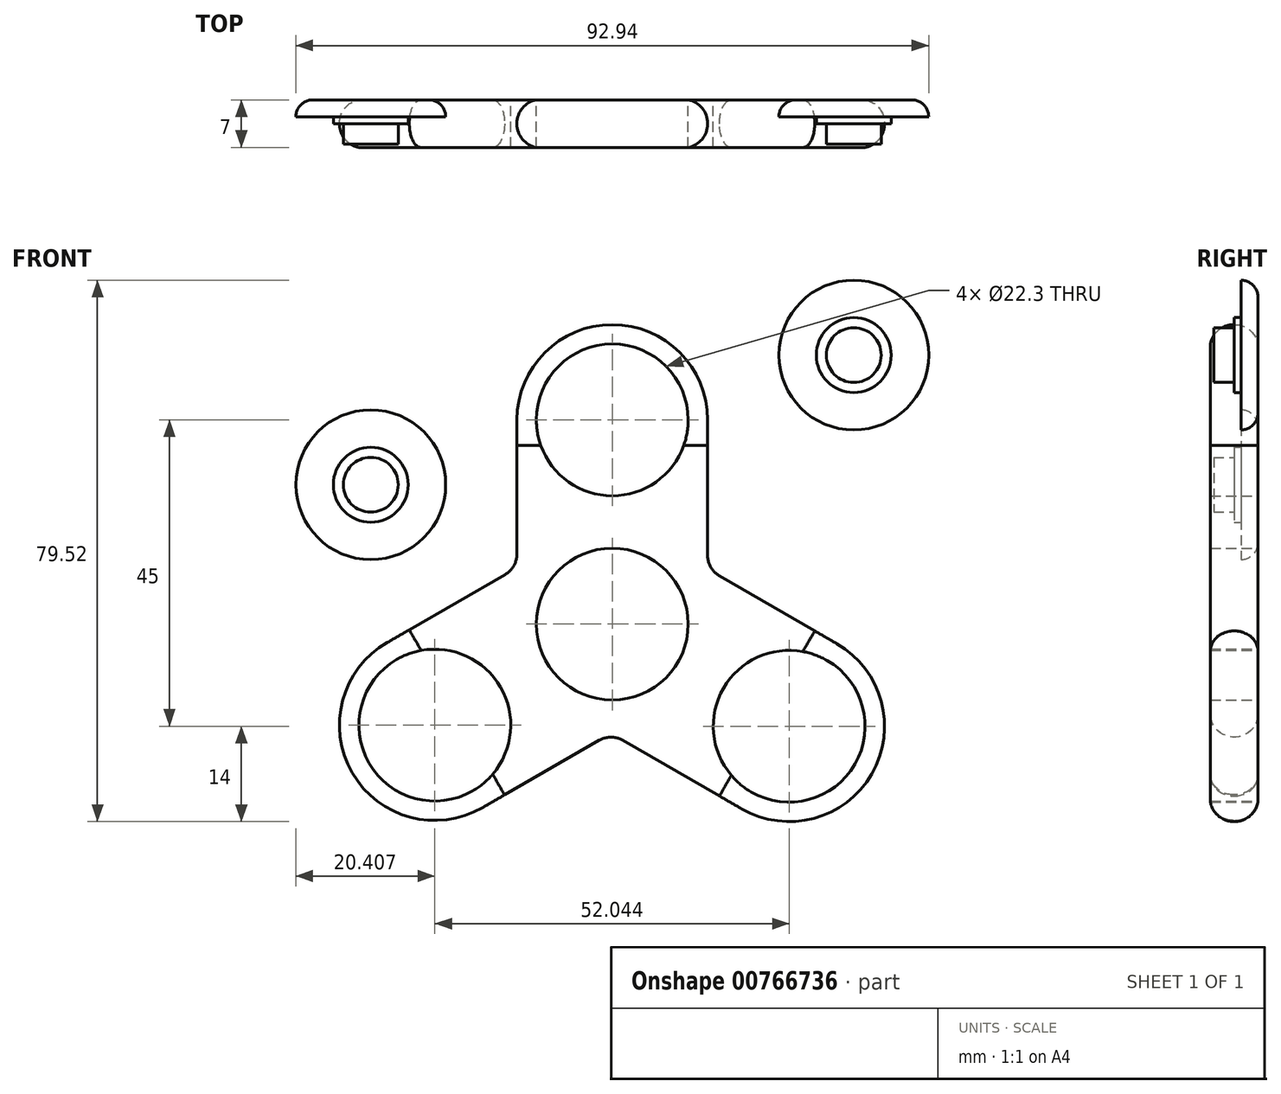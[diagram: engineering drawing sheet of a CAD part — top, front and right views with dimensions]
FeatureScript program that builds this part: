
annotation { "Feature Type Name" : "Feature", "Feature Type Description" : "" }
export const myFeature = defineFeature(function(context is Context, id is Id, definition is map)
    precondition{}
    {
        {
            var Q0;
            Q0=qCreatedBy(makeId("Front.planeOp"),FACE);
            var sketch = newSketch(context, id + "F0", { "sketchPlane" : qUnion([Q0])});
            skLineSegment(sketch, "E0.left", {"start": v(-14, -6.7) * mm, "end": v(-14, 15) * mm});
            skLineSegment(sketch, "E0.right", {"start": v(14, -6.92) * mm, "end": v(14, 15) * mm});
            skPoint(sketch, "E0.middle", {"position": v(0, 0) * mm});
            skArc(sketch, "E1", {"start": v(14, 15) * mm, "mid": v(0, 29) * mm, "end": v(-14, 15) * mm});
            skLineSegment(sketch, "E2.right", {"start": v(-0.18, -31.06) * mm, "end": v(18.98, -42.12) * mm});
            skArc(sketch, "E3", {"start": v(18.98, -42.12) * mm, "mid": v(38.1, -37) * mm, "end": v(32.98, -17.88) * mm});
            skLineSegment(sketch, "E4.right", {"start": v(-14, -6.7) * mm, "end": v(-33.06, -17.71) * mm});
            skArc(sketch, "E5", {"start": v(-33.06, -17.71) * mm, "mid": v(-38.19, -36.84) * mm, "end": v(-19.06, -41.96) * mm});
            skLineSegment(sketch, "E6.trimOffspring", {"start": v(-0.18, -31.06) * mm, "end": v(-19.06, -41.96) * mm});
            skLineSegment(sketch, "E7.trimOffspring", {"start": v(14, -6.92) * mm, "end": v(32.98, -17.88) * mm});
            skCircle(sketch, "E8", {"center": v(0, -15) * mm, "radius": 11.15 * mm});
            skCircle(sketch, "E9", {"center": v(-26.06, -29.84) * mm, "radius": 11.15 * mm});
            skCircle(sketch, "E10", {"center": v(25.98, -30) * mm, "radius": 11.15 * mm});
            skCircle(sketch, "E11", {"center": v(0, 15) * mm, "radius": 11.15 * mm});
            skSolve(sketch);
        }
        {
            var Q0;
            Q0=makeQuery(id+"F0.imprint","IMPRINT",FACE,{"disambiguationData":[TD([[makeQuery(id+"F0.imprint","IMPRINT",EDGE,{"derivedFrom":sQuery(id+"F0.wireOp",EDGE,"E0.left")}),-1.0]])]});
            extrude(context, id + "F1", {"entities" : qUnion([Q0]), "depth" : 7 * mm, "offsetDistance" : 25 * mm});
        }
        {
            var Q0;
            Q0=qCreatedBy(makeId("Front.planeOp"),FACE);
            var sketch = newSketch(context, id + "F2", { "sketchPlane" : qUnion([Q0])});
            skCircle(sketch, "E12", {"center": v(35.47, 24.52) * mm, "radius": 11 * mm});
            skCircle(sketch, "E13", {"center": v(35.47, 24.52) * mm, "radius": 5.5 * mm});
            skCircle(sketch, "E14", {"center": v(35.47, 24.52) * mm, "radius": 4.03 * mm});
            skSolve(sketch);
        }
        {
            var Q0;
            Q0=makeQuery(id+"F2.imprint","IMPRINT",FACE,{"disambiguationData":[TD([[makeQuery(id+"F2.imprint","IMPRINT",EDGE,{"derivedFrom":sQuery(id+"F2.wireOp",EDGE,"E12")}),1.0]])]});
            extrude(context, id + "F3", {"entities" : qUnion([Q0]), "depth" : 2.5 * mm, "offsetDistance" : 25 * mm});
        }
        {
            var Q0;
            Q0=makeQuery(id+"F2.imprint","IMPRINT",FACE,{"disambiguationData":[TD([[makeQuery(id+"F2.imprint","IMPRINT",EDGE,{"derivedFrom":sQuery(id+"F2.wireOp",EDGE,"E13")}),1.0]])]});
            extrude(context, id + "F4", {"entities" : qUnion([Q0]), "operationType" : NewBodyOperationType.ADD, "depth" : 3.5 * mm, "offsetDistance" : 25 * mm});
        }
        {
            var Q0;
            Q0=makeQuery(id+"F2.imprint","IMPRINT",FACE,{"disambiguationData":[TD([[makeQuery(id+"F2.imprint","IMPRINT",EDGE,{"derivedFrom":sQuery(id+"F2.wireOp",EDGE,"E14")}),1.0]])]});
            extrude(context, id + "F5", {"entities" : qUnion([Q0]), "operationType" : NewBodyOperationType.ADD, "depth" : 6.5 * mm, "offsetDistance" : 25 * mm});
        }
        {
            var Q0;
            Q0=makeQuery(id+"F1.opExtrude","SWEPT_FACE",FACE,{"disambiguationData":[OSD([sQuery(id+"F0.wireOp",EDGE,"E0.left")])]});
            var Q1;
            Q1=makeQuery(id+"F1.opExtrude","SWEPT_FACE",FACE,{"disambiguationData":[OSD([sQuery(id+"F0.wireOp",EDGE,"E4.right")])]});
            var Q2;
            Q2=makeQuery(id+"F1.opExtrude","SWEPT_FACE",FACE,{"disambiguationData":[OSD([sQuery(id+"F0.wireOp",EDGE,"E5")])]});
            var Q3;
            Q3=makeQuery(id+"F1.opExtrude","SWEPT_FACE",FACE,{"disambiguationData":[OSD([sQuery(id+"F0.wireOp",EDGE,"E1")])]});
            var Q4;
            Q4=makeQuery(id+"F1.opExtrude","SWEPT_FACE",FACE,{"disambiguationData":[OSD([sQuery(id+"F0.wireOp",EDGE,"E6.trimOffspring")])]});
            var Q5;
            Q5=makeQuery(id+"F1.opExtrude","SWEPT_FACE",FACE,{"disambiguationData":[OSD([sQuery(id+"F0.wireOp",EDGE,"E3")])]});
            var Q6;
            Q6=makeQuery(id+"F1.opExtrude","SWEPT_FACE",FACE,{"disambiguationData":[OSD([sQuery(id+"F0.wireOp",EDGE,"E2.right")])]});
            var Q7;
            Q7=makeQuery(id+"F1.opExtrude","SWEPT_FACE",FACE,{"disambiguationData":[OSD([sQuery(id+"F0.wireOp",EDGE,"E7.trimOffspring")])]});
            var Q8;
            Q8=makeQuery(id+"F1.opExtrude","SWEPT_FACE",FACE,{"disambiguationData":[OSD([sQuery(id+"F0.wireOp",EDGE,"E0.right")])]});
            fillet(context, id + "F6", {"entities" : qUnion([Q0, Q1, Q2, Q3, Q4, Q5, Q6, Q7, Q8]), "radius" : 3.5 * mm, "tangentPropagation" : true, "allowEdgeOverflow" : false});
        }
        {
            var Q0;
            Q0=makeQuery(id+"F3.opExtrude","CAP_EDGE",EDGE,{"disambiguationData":[OSD([sQuery(id+"F2.wireOp",EDGE,"E12")])],"isStart":true});
            fillet(context, id + "F7", {"entities" : qUnion([Q0]), "radius" : 2.5 * mm, "tangentPropagation" : true, "allowEdgeOverflow" : false});
        }
        {
            var Q0;
            Q0=makeQuery(id+"F3.opExtrude","SWEPT_BODY",BODY,{"disambiguationData":[OSD([sQuery(id+"F2.wireOp",EDGE,"E12"),sQuery(id+"F2.wireOp",EDGE,"E13")])]});
            var Q1;
            Q1=sQuery(id+"F0.wireOp",EDGE,"E11");
            circularPattern(context, id + "F8", {"entities" : qUnion([Q0]), "axis" : qUnion([Q1]), "angle" : 360 * degree, "instanceCount" : 2, "equalSpace" : true});
        }
    });
